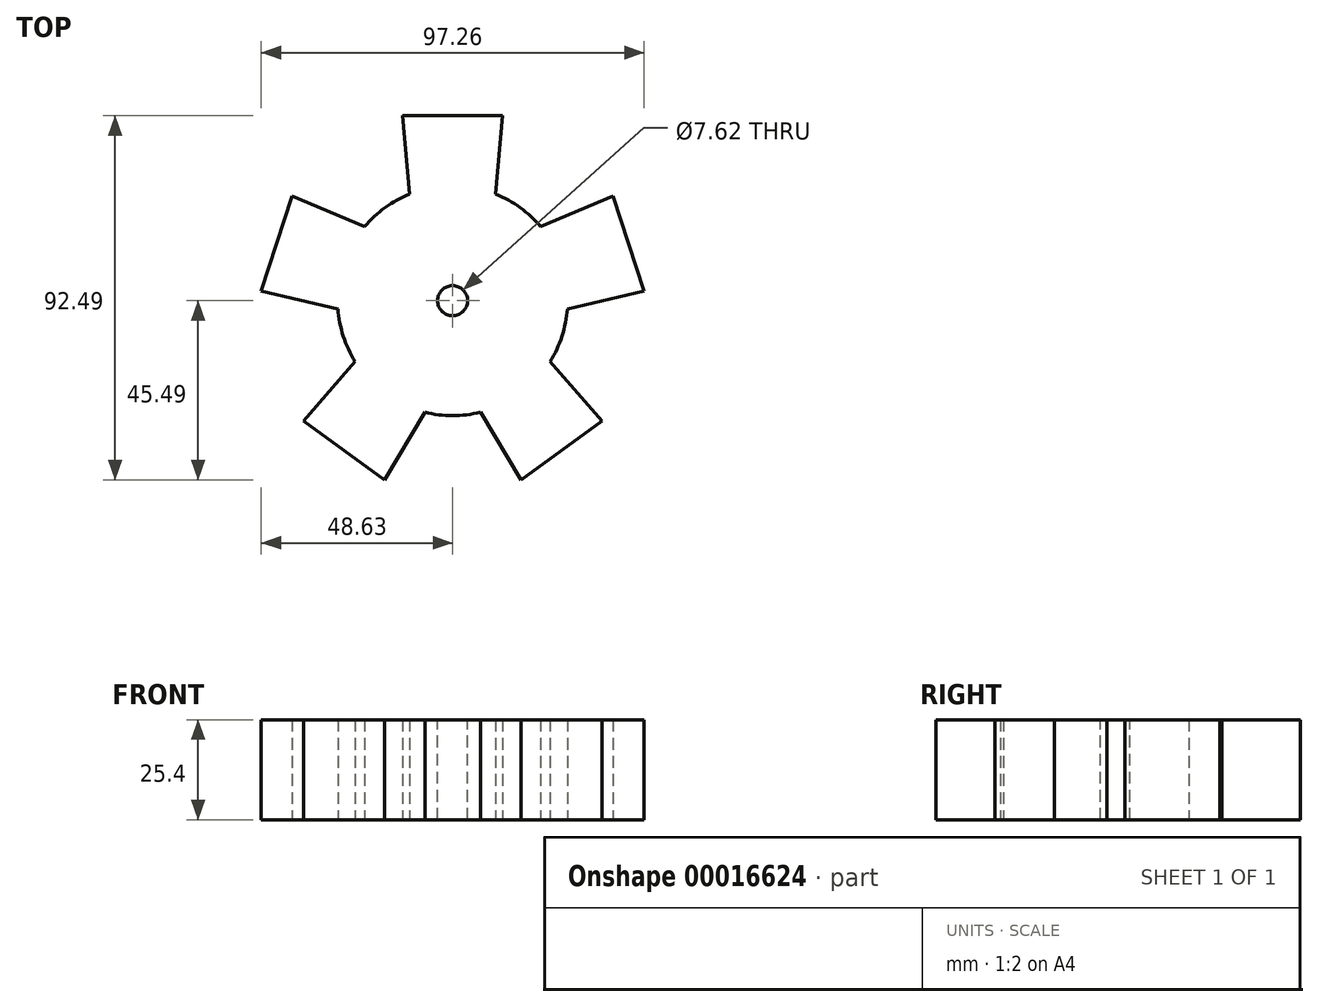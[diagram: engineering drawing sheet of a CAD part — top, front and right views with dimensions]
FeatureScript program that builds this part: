
annotation { "Feature Type Name" : "Feature", "Feature Type Description" : "" }
export const myFeature = defineFeature(function(context is Context, id is Id, definition is map)
    precondition{}
    {
        {
            var Q0;
            Q0=qCreatedBy(makeId("Top.planeOp"),FACE);
            var sketch = newSketch(context, id + "F0", { "sketchPlane" : qUnion([Q0])});
            skCircle(sketch, "E0", {"center": v(0, 0) * mm, "radius": 29.2 * mm});
            skLineSegment(sketch, "E1", {"start": v(0, 0) * mm, "end": v(0, 29.2) * mm, "construction": true});
            skLineSegment(sketch, "E2", {"start": v(-10.96, 27.07) * mm, "end": v(-12.7, 47) * mm});
            skLineSegment(sketch, "E3", {"start": v(-12.7, 47) * mm, "end": v(0, 47) * mm});
            skLineSegment(sketch, "E4.MirrorCS", {"start": v(10.96, 27.07) * mm, "end": v(12.7, 47) * mm});
            skLineSegment(sketch, "E5.MirrorCS", {"start": v(12.7, 47) * mm, "end": v(0, 47) * mm});
            skLineSegment(sketch, "E6.1.0", {"start": v(-29.13, -2.05) * mm, "end": v(-48.63, 2.45) * mm});
            skLineSegment(sketch, "E6.1.1", {"start": v(-48.63, 2.45) * mm, "end": v(-44.7, 14.52) * mm});
            skLineSegment(sketch, "E6.1.2", {"start": v(-40.78, 26.6) * mm, "end": v(-44.7, 14.52) * mm});
            skLineSegment(sketch, "E6.1.3", {"start": v(-22.36, 18.79) * mm, "end": v(-40.78, 26.6) * mm});
            skLineSegment(sketch, "E6.2.0", {"start": v(-7.05, -28.34) * mm, "end": v(-17.35, -45.5) * mm});
            skLineSegment(sketch, "E6.2.1", {"start": v(-17.35, -45.5) * mm, "end": v(-27.63, -38.03) * mm});
            skLineSegment(sketch, "E6.2.2", {"start": v(-37.9, -30.56) * mm, "end": v(-27.63, -38.03) * mm});
            skLineSegment(sketch, "E6.2.3", {"start": v(-24.78, -15.46) * mm, "end": v(-37.9, -30.56) * mm});
            skLineSegment(sketch, "E6.3.0", {"start": v(24.78, -15.46) * mm, "end": v(37.9, -30.56) * mm});
            skLineSegment(sketch, "E6.3.1", {"start": v(37.9, -30.56) * mm, "end": v(27.63, -38.03) * mm});
            skLineSegment(sketch, "E6.3.2", {"start": v(17.35, -45.5) * mm, "end": v(27.63, -38.03) * mm});
            skLineSegment(sketch, "E6.3.3", {"start": v(7.05, -28.34) * mm, "end": v(17.35, -45.5) * mm});
            skLineSegment(sketch, "E6.4.0", {"start": v(22.36, 18.79) * mm, "end": v(40.78, 26.6) * mm});
            skLineSegment(sketch, "E6.4.1", {"start": v(40.78, 26.6) * mm, "end": v(44.7, 14.52) * mm});
            skLineSegment(sketch, "E6.4.2", {"start": v(48.63, 2.45) * mm, "end": v(44.7, 14.52) * mm});
            skLineSegment(sketch, "E6.4.3", {"start": v(29.13, -2.05) * mm, "end": v(48.63, 2.45) * mm});
            skSolve(sketch);
        }
        {
            var Q0;
            Q0=qSketchRegion(id+"F0",true);
            extrude(context, id + "F1", {"entities" : qUnion([Q0]), "depth" : 25.4 * mm});
        }
        {
            var Q0;
            Q0=makeQuery(id+"F1.opExtrude","CAP_FACE",FACE,{"disambiguationData":[OSD([sQuery(id+"F0.wireOp",EDGE,"E0"),sQuery(id+"F0.wireOp",EDGE,"E2"),sQuery(id+"F0.wireOp",EDGE,"E3"),sQuery(id+"F0.wireOp",EDGE,"E4.MirrorCS"),sQuery(id+"F0.wireOp",EDGE,"E5.MirrorCS"),sQuery(id+"F0.wireOp",EDGE,"E6.1.0"),sQuery(id+"F0.wireOp",EDGE,"E6.1.1"),sQuery(id+"F0.wireOp",EDGE,"E6.1.2"),sQuery(id+"F0.wireOp",EDGE,"E6.1.3"),sQuery(id+"F0.wireOp",EDGE,"E6.2.0"),sQuery(id+"F0.wireOp",EDGE,"E6.2.1"),sQuery(id+"F0.wireOp",EDGE,"E6.2.2"),sQuery(id+"F0.wireOp",EDGE,"E6.2.3"),sQuery(id+"F0.wireOp",EDGE,"E6.3.0"),sQuery(id+"F0.wireOp",EDGE,"E6.3.1"),sQuery(id+"F0.wireOp",EDGE,"E6.3.2"),sQuery(id+"F0.wireOp",EDGE,"E6.3.3"),sQuery(id+"F0.wireOp",EDGE,"E6.4.0"),sQuery(id+"F0.wireOp",EDGE,"E6.4.1"),sQuery(id+"F0.wireOp",EDGE,"E6.4.2"),sQuery(id+"F0.wireOp",EDGE,"E6.4.3"),sQuery(id+"F0.wireOp",EDGE,"E6.5.0"),sQuery(id+"F0.wireOp",EDGE,"E6.5.1"),sQuery(id+"F0.wireOp",EDGE,"E6.5.2"),sQuery(id+"F0.wireOp",EDGE,"E6.5.3"),sQuery(id+"F0.wireOp",EDGE,"E6.6.0"),sQuery(id+"F0.wireOp",EDGE,"E6.6.1"),sQuery(id+"F0.wireOp",EDGE,"E6.6.2"),sQuery(id+"F0.wireOp",EDGE,"E6.6.3"),sQuery(id+"F0.wireOp",EDGE,"E6.7.0"),sQuery(id+"F0.wireOp",EDGE,"E6.7.1"),sQuery(id+"F0.wireOp",EDGE,"E6.7.2"),sQuery(id+"F0.wireOp",EDGE,"E6.7.3")])],"isStart":false});
            var sketch = newSketch(context, id + "F2", { "sketchPlane" : qUnion([Q0])});
            skCircle(sketch, "E7", {"center": v(0, 0) * mm, "radius": 3.81 * mm});
            skSolve(sketch);
        }
        {
            var Q0;
            Q0 = qSketchRegion(id + "F2", true);
            var Q1;
            Q1=makeQuery(id+"F2.imprint","IMPRINT",FACE,{"disambiguationData":[TD([[makeQuery(id+"F2.imprint","IMPRINT",EDGE,{"derivedFrom":sQuery(id+"F2.wireOp",EDGE,"E7")}),1.0]])]});
            extrude(context, id + "F3", {"entities" : qUnion([Q0, Q1]), "operationType" : NewBodyOperationType.REMOVE, "endBound" : BoundingType.THROUGH_ALL, "oppositeDirection" : true, "depth" : 25.4 * mm});
        }
    });
